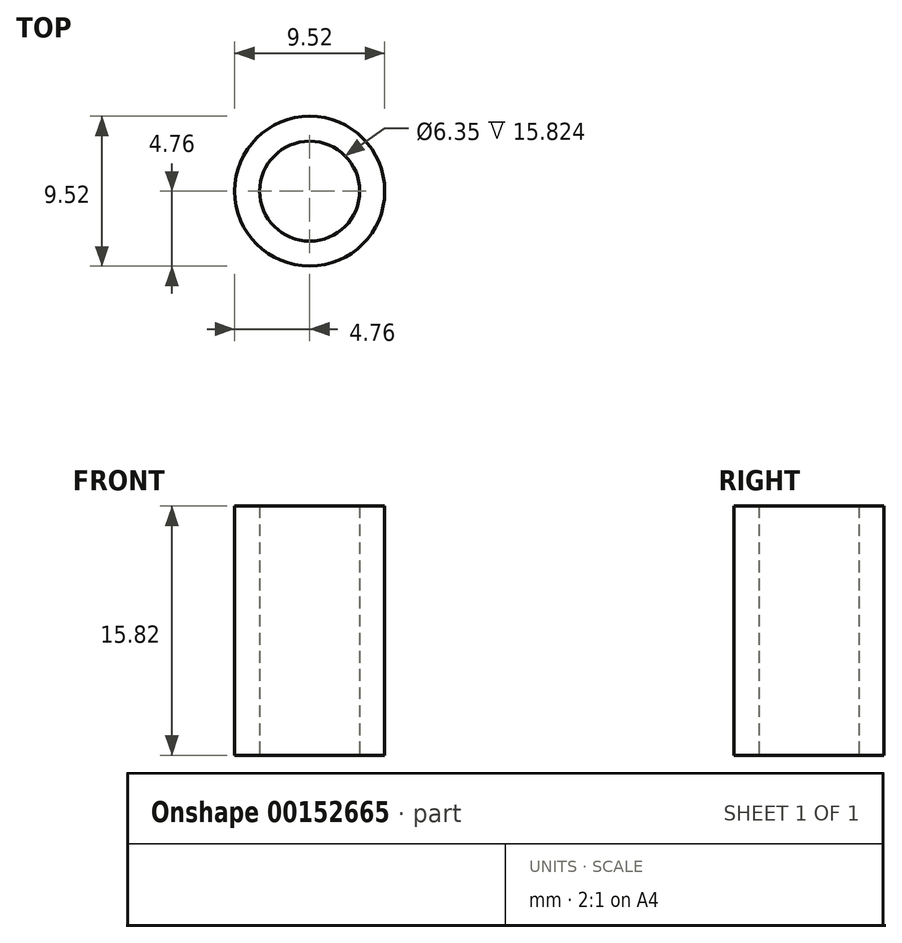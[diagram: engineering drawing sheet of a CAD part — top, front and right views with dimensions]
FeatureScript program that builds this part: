
annotation { "Feature Type Name" : "Feature", "Feature Type Description" : "" }
export const myFeature = defineFeature(function(context is Context, id is Id, definition is map)
    precondition{}
    {
        {
            var Q0;
            Q0=qCreatedBy(makeId("Top.planeOp"),FACE);
            var sketch = newSketch(context, id + "F0", { "sketchPlane" : qUnion([Q0])});
            skCircle(sketch, "E0", {"center": v(0, 0) * mm, "radius": 3.18 * mm});
            skCircle(sketch, "E1", {"center": v(0, 0) * mm, "radius": 4.76 * mm});
            skSolve(sketch);
        }
        {
            var Q0;
            Q0 = qSketchRegion(id + "F0", true);
            extrude(context, id + "F1", {"entities" : qUnion([Q0]), "depth" : 15.82 * mm});
        }
    });
